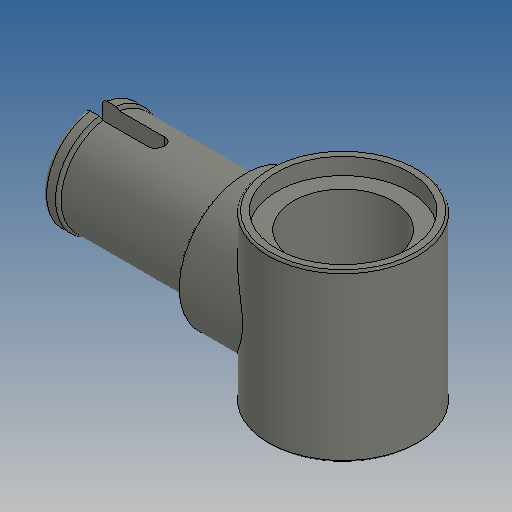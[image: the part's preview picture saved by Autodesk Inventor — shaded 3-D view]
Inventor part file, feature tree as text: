
AUTODESK INVENTOR PART (.ipt)
format: ipt  version: 2025 (Build 290162010, 162A)  size: 311,296 bytes
history: native  units: mm
features: extrude x4, sketch x4, mirror x1, revolve x1, fillet x1, projected_geometry x1
ambient origin geometry x8: Origin, YZ Plane, XZ Plane, XY Plane, X Axis, Y Axis, Z Axis, Center Point
bodies: Solid1 (feature_tree)
feature tree (12):
  extrude  "Extrusion1"  Depth=0.8mm TaperAngle=0.0deg
  extrude  "Extrusion7"  Depth=6.4mm
  mirror  "Mirror1"
  sketch  "Sketch7"  dims[d50=4.8mm d53=7.2mm]
  revolve  "Revolution1"  [1 undecoded]
  extrude  "Extrusion9"  Depth=0.2mm
  extrude  "Extrusion10"  Depth=0.2mm
  fillet  "Fillet2"  Radius=0.8mm
  sketch  "Sketch1"  dims[d14=8.0mm d15=0.0mm d41=0.8mm d42=0.0mm]
  sketch  "Sketch6"  dims[d48=7.2mm d49=6.4mm]
  sketch  "Sketch8"  dims[d54=0.8mm d55=4.8mm d58=3.4mm d59=0.8mm d60=90.0deg d62=6.4mm d63=3.2mm d64=5.0mm d65=4.8mm d66=10.0mm d67=0.0mm d68=10.0mm d69=0.0mm d70=0.1mm d71=0.0mm d73=0.2mm]
  projected_geometry  "Projected Loop3"
note: 1 required parameter value undecoded (feature->parameter linkage not recoverable at this tier; creation-order binding heuristic only, values carry confidence <= 0.55)
